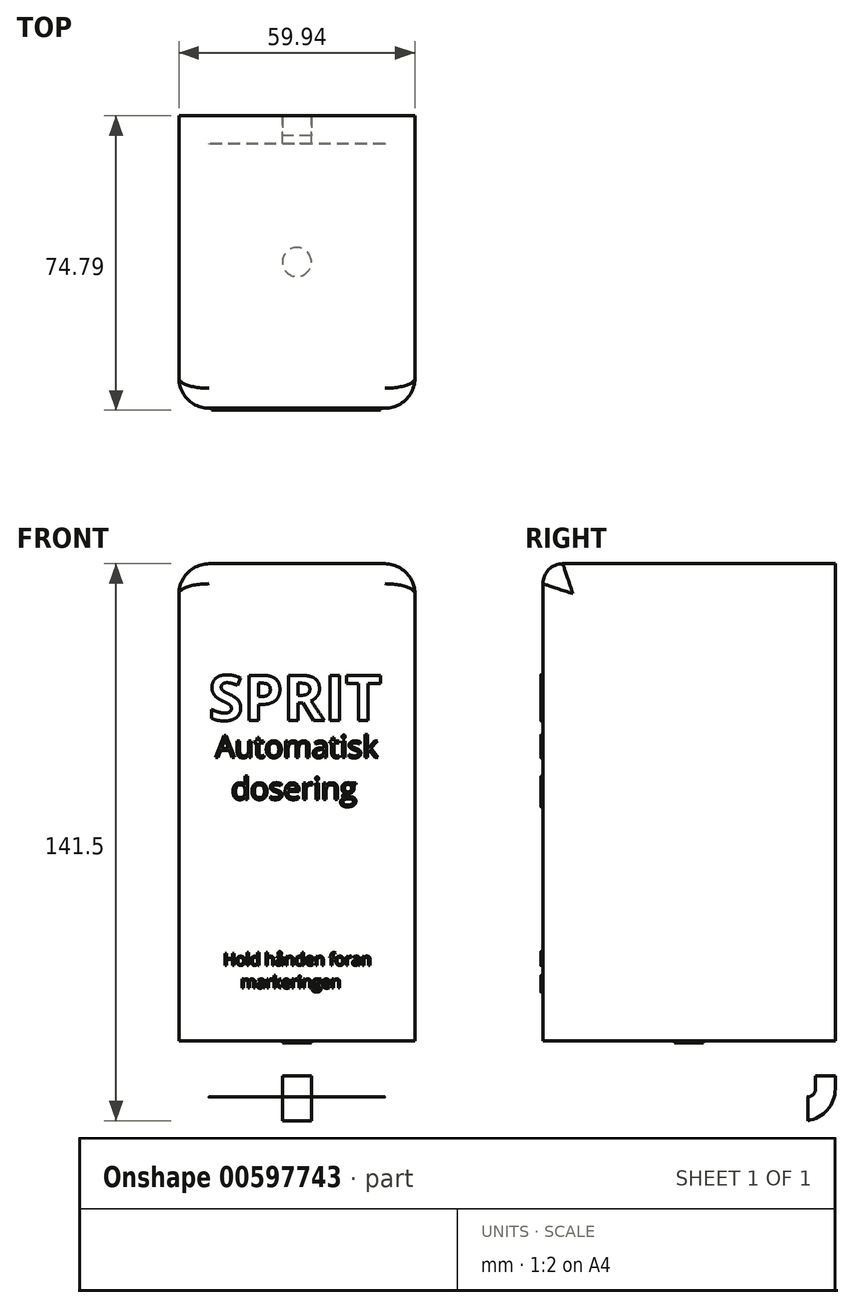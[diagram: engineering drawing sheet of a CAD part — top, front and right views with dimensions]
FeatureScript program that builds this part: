
annotation { "Feature Type Name" : "Feature", "Feature Type Description" : "" }
export const myFeature = defineFeature(function(context is Context, id is Id, definition is map)
    precondition{}
    {
        {
            var Q0;
            Q0=qCreatedBy(makeId("Right.planeOp"),FACE);
            var sketch = newSketch(context, id + "F0", { "sketchPlane" : qUnion([Q0])});
            skLineSegment(sketch, "E0.bottom", {"start": v(37.14, 60.63) * mm, "end": v(-37.14, 60.63) * mm});
            skLineSegment(sketch, "E0.top", {"start": v(37.14, -60.63) * mm, "end": v(-37.14, -60.63) * mm});
            skLineSegment(sketch, "E0.left", {"start": v(37.14, 60.63) * mm, "end": v(37.14, -60.63) * mm});
            skLineSegment(sketch, "E0.right", {"start": v(-37.14, 60.63) * mm, "end": v(-37.14, -60.63) * mm});
            skPoint(sketch, "E0.middle", {"position": v(0, 0) * mm});
            skLineSegment(sketch, "E1.bottom", {"start": v(37.14, -60.63) * mm, "end": v(27.15, -60.63) * mm});
            skPoint(sketch, "E2.oppositeSnap0", {"position": v(32.15, -60.63) * mm});
            skLineSegment(sketch, "E2.bottom", {"start": v(37.14, -60.63) * mm, "end": v(32.15, -60.63) * mm});
            skLineSegment(sketch, "E2.top", {"start": v(37.14, -69.47) * mm, "end": v(32.15, -69.47) * mm});
            skLineSegment(sketch, "E2.left", {"start": v(37.14, -60.63) * mm, "end": v(37.14, -69.47) * mm});
            skLineSegment(sketch, "E2.right", {"start": v(32.15, -60.63) * mm, "end": v(32.15, -69.47) * mm});
            skLineSegment(sketch, "E3.bottom", {"start": v(30.14, -74.86) * mm, "end": v(24.48, -74.86) * mm});
            skLineSegment(sketch, "E3.top", {"start": v(30.14, -80.87) * mm, "end": v(24.48, -80.87) * mm});
            skLineSegment(sketch, "E3.left", {"start": v(30.14, -74.86) * mm, "end": v(30.14, -80.87) * mm});
            skLineSegment(sketch, "E3.right", {"start": v(24.48, -74.86) * mm, "end": v(24.48, -80.87) * mm});
            skLineSegment(sketch, "E4", {"start": v(32.15, -69.47) * mm, "end": v(32.15, -72.79) * mm});
            skArc(sketch, "E5", {"start": v(29.94, -74.86) * mm, "mid": v(31.5, -74.3) * mm, "end": v(32.15, -72.79) * mm});
            skLineSegment(sketch, "E6", {"start": v(29.94, -74.86) * mm, "end": v(30.14, -74.86) * mm});
            skLineSegment(sketch, "E7", {"start": v(37.14, -69.47) * mm, "end": v(37.14, -72.85) * mm});
            skLineSegment(sketch, "E8", {"start": v(30.14, -80.87) * mm, "end": v(30.14, -80.87) * mm});
            skArc(sketch, "E9", {"start": v(30.14, -80.87) * mm, "mid": v(35.14, -78.17) * mm, "end": v(37.14, -72.85) * mm});
            skSolve(sketch);
        }
        {
            var Q0;
            Q0=makeQuery(id+"F0.imprint","IMPRINT",FACE,{"disambiguationData":[TD([[makeQuery(id+"F0.imprint","IMPRINT",EDGE,{"derivedFrom":sQuery(id+"F0.wireOp",EDGE,"E0.bottom")}),1.0]])]});
            extrude(context, id + "F1", {"entities" : qUnion([Q0]), "endBound" : BoundingType.SYMMETRIC, "oppositeDirection" : true, "depth" : 59.94 * mm, "offsetDistance" : 25.4 * mm});
        }
        {
            var Q0;
            Q0=makeQuery(id+"F1.opExtrude","CAP_EDGE",EDGE,{"disambiguationData":[OSD([sQuery(id+"F0.wireOp",EDGE,"E0.bottom")])],"isStart":false});
            var Q1;
            Q1=makeQuery(id+"F1.opExtrude","CAP_EDGE",EDGE,{"disambiguationData":[OSD([sQuery(id+"F0.wireOp",EDGE,"E0.right")])],"isStart":false});
            var Q2;
            Q2=makeQuery(id+"F1.opExtrude","CAP_EDGE",EDGE,{"disambiguationData":[OSD([sQuery(id+"F0.wireOp",EDGE,"E0.bottom")])],"isStart":true});
            var Q3;
            Q3=makeQuery(id+"F1.opExtrude","CAP_EDGE",EDGE,{"disambiguationData":[OSD([sQuery(id+"F0.wireOp",EDGE,"E0.right")])],"isStart":true});
            fillet(context, id + "F2", {"entities" : qUnion([Q0, Q1, Q2, Q3]), "radius" : 7.62 * mm, "tangentPropagation" : true, "allowEdgeOverflow" : false});
        }
        {
            var Q0;
            Q0=makeQuery(id+"F1.opExtrude","SWEPT_EDGE",EDGE,{"disambiguationData":[OSD([sQuery(id+"F0.wireOp",EDGE,"E0.bottom"),sQuery(id+"F0.wireOp",EDGE,"E0.right")])]});
            fillet(context, id + "F3", {"entities" : qUnion([Q0]), "radius" : 5.08 * mm, "tangentPropagation" : true, "allowEdgeOverflow" : false});
        }
        {
            var Q0;
            Q0=makeQuery(id+"F0.imprint","IMPRINT",FACE,{"disambiguationData":[TD([[makeQuery(id+"F0.imprint","IMPRINT",EDGE,{"derivedFrom":sQuery(id+"F0.wireOp",EDGE,"E2.bottom")}),1.0]])]});
            var sketch = newSketch(context, id + "F4", { "sketchPlane" : qUnion([Q0])});
            skLineSegment(sketch, "E10", {"start": v(37.8, -61.37) * mm, "end": v(37.8, -69.81) * mm});
            skSolve(sketch);
        }
        {
            var Q0;
            Q0=makeQuery(id+"F4.imprint","IMPRINT",FACE,{"disambiguationData":[TD([[makeQuery(id+"F4.imprint","IMPRINT",EDGE,{"derivedFrom":makeQuery(id+"F0.imprint","IMPRINT",EDGE,{"derivedFrom":sQuery(id+"F0.wireOp",EDGE,"E2.bottom")})}),1.0]])]});
            var Q1;
            Q1=makeQuery(id+"F0.imprint","IMPRINT",FACE,{"disambiguationData":[TD([[makeQuery(id+"F0.imprint","IMPRINT",EDGE,{"derivedFrom":sQuery(id+"F0.wireOp",EDGE,"E2.top")}),1.0]])]});
            extrude(context, id + "F5", {"entities" : qUnion([Q0, Q1]), "operationType" : NewBodyOperationType.ADD, "endBound" : BoundingType.SYMMETRIC, "depth" : 7.37 * mm, "offsetDistance" : 25.4 * mm});
        }
        {
            var Q0;
            {var subQ4=sQuery(id+"F0.wireOp",EDGE,"E3.bottom");Q0=makeQuery(id+"F0.imprint","IMPRINT",FACE,{"disambiguationData":[TD([[makeQuery(id+"F0.imprint","IMPRINT",EDGE,{"derivedFrom":subQ4}),1.0]])]});}
            extrude(context, id + "F6", {"entities" : qUnion([Q0]), "operationType" : NewBodyOperationType.ADD, "endBound" : BoundingType.SYMMETRIC, "depth" : 44.7 * mm, "offsetDistance" : 25.4 * mm});
        }
        {
            var Q0;
            Q0=makeQuery(id+"F1.opExtrude","SWEPT_FACE",FACE,{"disambiguationData":[OSD([sQuery(id+"F0.wireOp",EDGE,"E0.top"),sQuery(id+"F0.wireOp",EDGE,"E1.bottom"),sQuery(id+"F0.wireOp",EDGE,"E2.bottom")])]});
            var sketch = newSketch(context, id + "F7", { "sketchPlane" : qUnion([Q0])});
            skPoint(sketch, "E11.oppositeSnap0", {"position": v(-29.97, -3.81) * mm});
            skLineSegment(sketch, "E11.bottom", {"start": v(-29.97, -60.63) * mm, "end": v(-29.97, -60.63) * mm});
            skLineSegment(sketch, "E11.top", {"start": v(-29.97, -62.51) * mm, "end": v(-29.97, -62.51) * mm});
            skLineSegment(sketch, "E11.left", {"start": v(-29.97, -60.63) * mm, "end": v(-29.97, -62.51) * mm});
            skLineSegment(sketch, "E11.right", {"start": v(-29.97, -60.63) * mm, "end": v(-29.97, -62.51) * mm});
            skCircle(sketch, "E12", {"center": v(0, 0) * mm, "radius": 3.68 * mm});
            skSolve(sketch);
        }
        {
            var Q0;
            Q0=makeQuery(id+"F7.imprint","IMPRINT",FACE,{"disambiguationData":[TD([[makeQuery(id+"F7.imprint","IMPRINT",EDGE,{"derivedFrom":sQuery(id+"F7.wireOp",EDGE,"E12")}),1.0]])]});
            extrude(context, id + "F8", {"entities" : qUnion([Q0]), "operationType" : NewBodyOperationType.ADD, "depth" : 0.5 * mm, "offsetDistance" : 25.4 * mm});
        }
        {
            var Q0;
            Q0=makeQuery(id+"F1.opExtrude","SWEPT_FACE",FACE,{"disambiguationData":[OSD([sQuery(id+"F0.wireOp",EDGE,"E0.right")])]});
            var sketch = newSketch(context, id + "F9", { "sketchPlane" : qUnion([Q0])});
            skText(sketch, "E13", { "text": "SPRIT", "fontName": "OpenSans-Bold.ttf"});
            const initialGuessF9  = {"E13": [-0.02246, 0.02084, 1, 0, 0.01152]};
            skSetInitialGuess(sketch, initialGuessF9);
            skSolve(sketch);
        }
        {
            var Q0;
            Q0=makeQuery(id+"F9.imprint","IMPRINT",FACE,{"disambiguationData":[TD([[makeQuery(id+"F9.imprint","IMPRINT",EDGE,{"derivedFrom":sQuery(id+"F9.wireOp",EDGE,"E13.sketch_text.stroke-0")}),1.0]])]});
            var sketch = newSketch(context, id + "F10", { "sketchPlane" : qUnion([Q0])});
            skText(sketch, "E14", { "text": "Automatisk\n  dosering", "fontName": "OpenSans-Regular.ttf"});
            const initialGuessF10  = {"E14": [-0.02074, 0.01137, 1, 0, 0.00563]};
            skSetInitialGuess(sketch, initialGuessF10);
            skSolve(sketch);
        }
        {
            var Q0;
            Q0=makeQuery(id+"F9.imprint","IMPRINT",FACE,{"disambiguationData":[TD([[makeQuery(id+"F9.imprint","IMPRINT",EDGE,{"derivedFrom":sQuery(id+"F9.wireOp",EDGE,"E13.sketch_text.stroke-0")}),1.0]])]});
            var sketch = newSketch(context, id + "F11", { "sketchPlane" : qUnion([Q0])});
            skText(sketch, "E15", { "text": "Hold hånden foran\n    markeringen", "fontName": "OpenSans-Regular.ttf"});
            const initialGuessF11  = {"E15": [-0.0187, -0.04139, 1, 0, 0.00307]};
            skSetInitialGuess(sketch, initialGuessF11);
            skSolve(sketch);
        }
        {
            var Q0;
            Q0=makeQuery(id+"F6.opExtrude","CAP_FACE",FACE,{"disambiguationData":[OSD([sQuery(id+"F0.wireOp",EDGE,"E3.bottom"),sQuery(id+"F0.wireOp",EDGE,"E3.top"),sQuery(id+"F0.wireOp",EDGE,"E3.left"),sQuery(id+"F0.wireOp",EDGE,"E3.right"),sQuery(id+"F0.wireOp",EDGE,"E5")])],"isStart":true});
            var sketch = newSketch(context, id + "F12", { "sketchPlane" : qUnion([Q0])});
            skLineSegment(sketch, "E16", {"start": v(-24.48, -74.86) * mm, "end": v(33.76, -74.86) * mm});
            skSolve(sketch);
        }
        {
            var Q0;
            Q0=sQuery(id+"F12.wireOp",EDGE,"E16");
            extrude(context, id + "F13", {"bodyType" : ToolBodyType.SURFACE, "surfaceEntities" : qUnion([Q0]), "oppositeDirection" : true, "depth" : 1.02 * mm, "offsetDistance" : 25.4 * mm});
        }
        {
            var Q0;
            Q0=makeQuery(id+"F6.opExtrude","CAP_FACE",FACE,{"disambiguationData":[OSD([sQuery(id+"F0.wireOp",EDGE,"E3.bottom"),sQuery(id+"F0.wireOp",EDGE,"E3.top"),sQuery(id+"F0.wireOp",EDGE,"E3.left"),sQuery(id+"F0.wireOp",EDGE,"E3.right"),sQuery(id+"F0.wireOp",EDGE,"E5")])],"isStart":false});
            var sketch = newSketch(context, id + "F14", { "sketchPlane" : qUnion([Q0])});
            skLineSegment(sketch, "E17", {"start": v(24.48, -74.86) * mm, "end": v(-38.53, -74.86) * mm});
            skLineSegment(sketch, "E18", {"start": v(-38.53, -74.86) * mm, "end": v(24.48, -74.86) * mm});
            skSolve(sketch);
        }
        {
            var Q0;
            Q0=sQuery(id+"F14.wireOp",EDGE,"E18");
            extrude(context, id + "F15", {"bodyType" : ToolBodyType.SURFACE, "surfaceEntities" : qUnion([Q0]), "depth" : 1.27 * mm, "offsetDistance" : 25.4 * mm});
        }
        {
            var Q0;
            Q0 = qSketchRegion(id + "F10", true);
            var Q1;
            Q1 = qSketchRegion(id + "F9", true);
            var Q2;
            Q2 = qSketchRegion(id + "F11", true);
            extrude(context, id + "F16", {"entities" : qUnion([Q0, Q1, Q2]), "operationType" : NewBodyOperationType.ADD, "depth" : 0.5 * mm, "offsetDistance" : 25.4 * mm});
        }
    });
